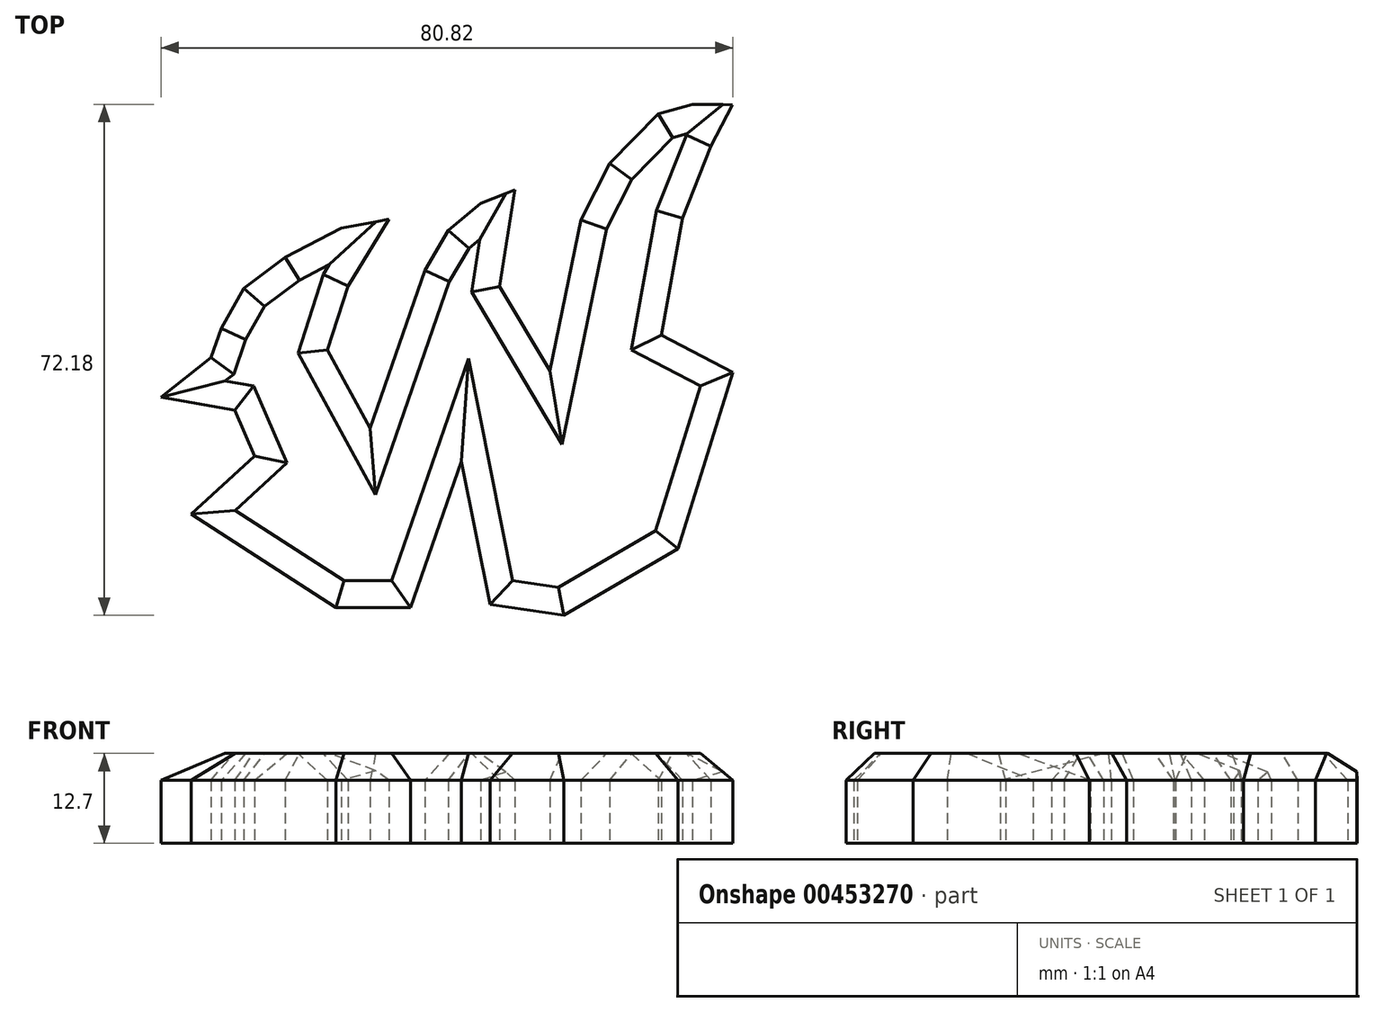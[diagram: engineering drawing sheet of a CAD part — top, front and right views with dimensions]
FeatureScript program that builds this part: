
annotation { "Feature Type Name" : "Feature", "Feature Type Description" : "" }
export const myFeature = defineFeature(function(context is Context, id is Id, definition is map)
    precondition{}
    {
        {
            var Q0;
            Q0=qCreatedBy(makeId("Top.planeOp"),FACE);
            var sketch = newSketch(context, id + "F0", { "sketchPlane" : qUnion([Q0])});
            skLineSegment(sketch, "E0", {"start": v(-66.57, -19.53) * mm, "end": v(-68, -23.7) * mm});
            skLineSegment(sketch, "E1", {"start": v(-50.33, -59) * mm, "end": v(-39.8, -59) * mm});
            skLineSegment(sketch, "E2", {"start": v(-39.8, -59) * mm, "end": v(-32.6, -38.3) * mm});
            skLineSegment(sketch, "E3", {"start": v(-32.6, -38.3) * mm, "end": v(-28.6, -58.5) * mm});
            skLineSegment(sketch, "E4", {"start": v(-28.6, -58.5) * mm, "end": v(-18.18, -60.07) * mm});
            skLineSegment(sketch, "E5", {"start": v(5.74, -25.74) * mm, "end": v(-4.4, -20.49) * mm});
            skLineSegment(sketch, "E6", {"start": v(-37.8, -11.33) * mm, "end": v(-45.53, -33.65) * mm});
            skLineSegment(sketch, "E7", {"start": v(-50.33, -59) * mm, "end": v(-70.8, -45.77) * mm});
            skLineSegment(sketch, "E8", {"start": v(-70.8, -45.77) * mm, "end": v(-61.83, -37.54) * mm});
            skLineSegment(sketch, "E9", {"start": v(-75.08, -29.27) * mm, "end": v(-68, -23.7) * mm});
            skLineSegment(sketch, "E10", {"start": v(-61.83, -37.54) * mm, "end": v(-64.63, -31.08) * mm});
            skLineSegment(sketch, "E11", {"start": v(-64.63, -31.08) * mm, "end": v(-75.08, -29.27) * mm});
            skLineSegment(sketch, "E12", {"start": v(-48.65, -13.54) * mm, "end": v(-51.57, -22.6) * mm});
            skLineSegment(sketch, "E13", {"start": v(-51.57, -22.6) * mm, "end": v(-45.53, -33.65) * mm});
            skLineSegment(sketch, "E14", {"start": v(-25.05, 0) * mm, "end": v(-27.2, -13.63) * mm});
            skLineSegment(sketch, "E15", {"start": v(-27.2, -13.63) * mm, "end": v(-20.14, -25.53) * mm});
            skLineSegment(sketch, "E16", {"start": v(-18.18, -60.07) * mm, "end": v(-2, -50.63) * mm});
            skLineSegment(sketch, "E17", {"start": v(-2, -50.63) * mm, "end": v(5.74, -25.74) * mm});
            skLineSegment(sketch, "E18", {"start": v(-37.8, -11.33) * mm, "end": v(-34.5, -5.71) * mm});
            skLineSegment(sketch, "E19", {"start": v(-66.57, -19.53) * mm, "end": v(-63.36, -13.86) * mm});
            skLineSegment(sketch, "E20", {"start": v(-63.36, -13.86) * mm, "end": v(-57.54, -9.47) * mm});
            skLineSegment(sketch, "E21", {"start": v(-57.54, -9.47) * mm, "end": v(-49.56, -5.38) * mm});
            skLineSegment(sketch, "E22", {"start": v(-49.56, -5.38) * mm, "end": v(-42.88, -4.12) * mm});
            skLineSegment(sketch, "E23", {"start": v(-42.88, -4.12) * mm, "end": v(-48.65, -13.54) * mm});
            skLineSegment(sketch, "E24", {"start": v(-34.5, -5.71) * mm, "end": v(-29.89, -1.91) * mm});
            skLineSegment(sketch, "E25", {"start": v(-29.89, -1.91) * mm, "end": v(-25.05, 0) * mm});
            skLineSegment(sketch, "E26", {"start": v(-20.14, -25.53) * mm, "end": v(-15.72, -4.26) * mm});
            skLineSegment(sketch, "E27", {"start": v(-15.72, -4.26) * mm, "end": v(-11.67, 3.75) * mm});
            skLineSegment(sketch, "E28", {"start": v(-11.67, 3.75) * mm, "end": v(-4.82, 10.75) * mm});
            skLineSegment(sketch, "E29", {"start": v(-4.82, 10.75) * mm, "end": v(0, 12.1) * mm});
            skLineSegment(sketch, "E30", {"start": v(0, 12.1) * mm, "end": v(5.67, 12.05) * mm});
            skLineSegment(sketch, "E31", {"start": v(5.67, 12.05) * mm, "end": v(2.64, 6.2) * mm});
            skLineSegment(sketch, "E32", {"start": v(2.64, 6.2) * mm, "end": v(-1.4, -3.98) * mm});
            skLineSegment(sketch, "E33", {"start": v(-1.4, -3.98) * mm, "end": v(-4.4, -20.49) * mm});
            skSolve(sketch);
        }
        {
            var Q0;
            Q0=qSketchRegion(id+"FpxrbdjMyEjlgeR_4",true);
            var Q1;
            Q1=qSketchRegion(id+"FhSuuO6UR1XzC2C_4",true);
            var Q2;
            Q2=qSketchRegion(id+"F0",true);
            var Q3;
            Q3=qSketchRegion(id+"FiezEiqxvGsPzSm_4",true);
            extrude(context, id + "F1", {"entities" : qUnion([Q0, Q1, Q2, Q3]), "depth" : 12.7 * mm});
        }
        {
            var Q0;
            Q0=makeQuery(id+"F1.opExtrude","CAP_FACE",FACE,{"disambiguationData":[OSD([sQuery(id+"F0.wireOp",EDGE,"E0"),sQuery(id+"F0.wireOp",EDGE,"1e08c8b1-9200-43e2-9ef8-3587783a8059"),sQuery(id+"F0.wireOp",EDGE,"E1"),sQuery(id+"F0.wireOp",EDGE,"E2"),sQuery(id+"F0.wireOp",EDGE,"E3"),sQuery(id+"F0.wireOp",EDGE,"E4"),sQuery(id+"F0.wireOp",EDGE,"0ce45ec2-a6e0-47d8-b840-3ec413a35b4f"),sQuery(id+"F0.wireOp",EDGE,"E5"),sQuery(id+"F0.wireOp",EDGE,"f3ba687f-88bf-4d00-8f6e-e38d44427f64"),sQuery(id+"F0.wireOp",EDGE,"2efff79b-ab16-429b-b17f-efade3c48f01"),sQuery(id+"F0.wireOp",EDGE,"2b46e4bb-6cc0-4f99-82fd-c8c5a52d1865"),sQuery(id+"F0.wireOp",EDGE,"70c9ad9f-9187-4193-a059-e092611d1764"),sQuery(id+"F0.wireOp",EDGE,"be855307-20ae-415d-9a71-00c6efc602dc"),sQuery(id+"F0.wireOp",EDGE,"E6"),sQuery(id+"F0.wireOp",EDGE,"26fa7675-7971-4662-972d-955d5f66880c"),sQuery(id+"F0.wireOp",EDGE,"2bc255a8-6b8b-490a-b790-fec38d9853a2")])],"isStart":false});
            chamfer(context, id + "F2", {"entities" : qUnion([Q0]), "width" : 3.8 * mm, "tangentPropagation" : true});
        }
    });
